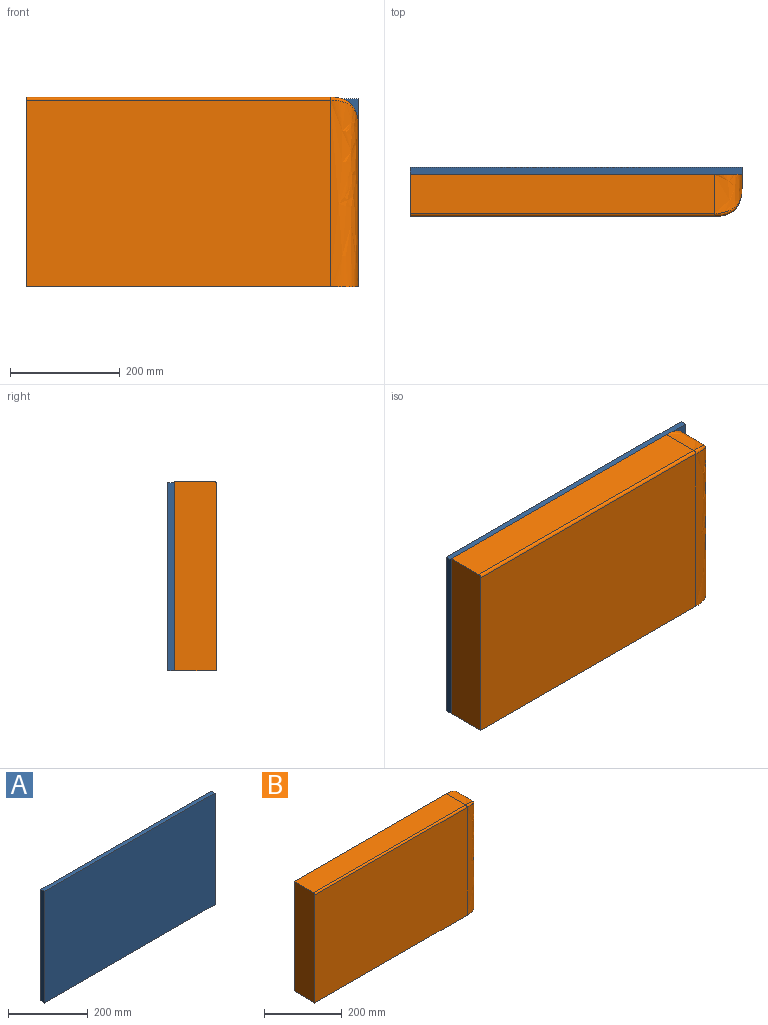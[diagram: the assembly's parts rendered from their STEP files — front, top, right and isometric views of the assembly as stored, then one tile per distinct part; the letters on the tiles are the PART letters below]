
ASSEMBLY  parts=2 mates=1
PART A: 6 faces, bbox 605.2x12.7x342.9 mm
  f0: plane 605.16x12.7mm, normal (0,0,-1), area 7685.5mm2, adj f1,f3,f4,f5
  f1: plane 342.9x12.7mm, normal (1,0,0), area 4354.8mm2, adj f0,f2,f4,f5
  f2: plane 605.16x12.7mm, normal (0,0,1), area 7685.5mm2, adj f1,f3,f4,f5
  f3: plane 342.9x12.7mm, normal (-1,0,0), area 4354.8mm2, adj f0,f2,f4,f5
  f4: plane 605.16x342.9mm, normal (0,-1,0), area 207507.6mm2, adj f0,f1,f2,f3
  f5: plane 605.16x342.9mm, normal (0,1,0), area 207507.6mm2, adj f0,f1,f2,f3
PART B: 10 faces, bbox 605.2x79.8x362.5 mm
  f0: plane 605.16x76.2mm, normal (0,0,-1), area 45682.7mm2, adj f1,f3,f4,f5,f9
  f1: plane 294.64x25.4mm, normal (1,0,0), area 7483.9mm2, adj f0,f5,f7,f9
  f2: plane 554.36x71.12mm, normal (0,0,1), area 39425.7mm2, adj f3,f5,f6,f7
  f3: plane 345.44x76.2mm, normal (-1,0,0), area 26317mm2, adj f0,f2,f4,f5,f6
  f4: plane 554.36x340.36mm, normal (0,-1,0), area 188680.3mm2, adj f0,f3,f6,f9
  f5: plane 605.16x345.44mm, normal (0,1,0), area 208614.6mm2, adj f0,f1,f2,f3,f7
  f6: cylinder r=5.08mm len=554.36mm, axis (1,0,0), area 4423.6mm2, adj f2,f3,f4,f8
  f7: bspline ~74.68x50.8mm, area 4594.8mm2, adj f1,f2,f5,f8
  f8: bspline ~71.36x50.8mm, area 301.7mm2, adj f6,f7,f9
  f9: bspline ~357.38x50.8mm, area 26796.2mm2, adj f0,f1,f4,f8
PLACE A t=(-2.1,-187.72,-126.44)mm
PLACE B t=(-2.1,-200.42,-126.44)mm
MATE fastened A.f4 <-> B.f5  axis (0,-1,0) through (-607.26,-200.42,-126.44)mm
